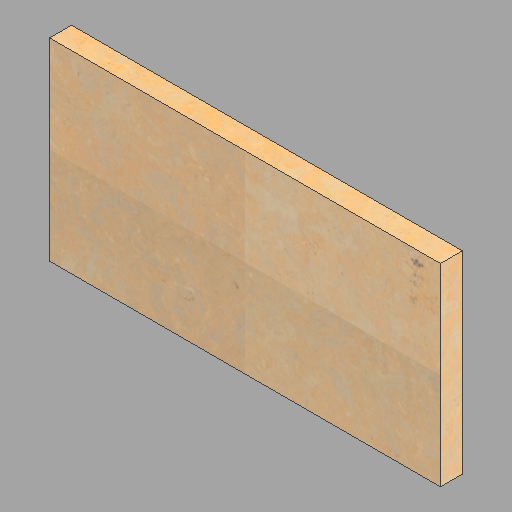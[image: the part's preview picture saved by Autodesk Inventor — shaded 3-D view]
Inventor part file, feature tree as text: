
AUTODESK INVENTOR PART (.ipt)
format: ipt  version: 2023 (Build 270158000, 158)  size: 289,792 bytes
history: native  units: in
note: dims shown in document units (in); Inventor stores cm internally (conversion verified against a paired STEP export)
features: other x1, extrude x1, sketch x1
ambient origin geometry x8: Origin, YZ Plane, XZ Plane, XY Plane, X Axis, Y Axis, Z Axis, Center Point
bodies: Solid1 (feature_tree)
feature tree (3):
  other  "13 - panel crnr - 195"
  extrude  "Extrusion1"  Depth=17.625in
  sketch  "Sketch1"  dims[d0=35.625in d1=17.625in d2=2.0in d3=0.0in]
